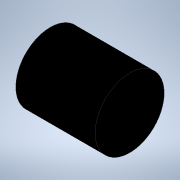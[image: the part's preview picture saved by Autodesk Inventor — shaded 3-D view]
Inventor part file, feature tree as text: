
AUTODESK INVENTOR PART (.ipt)
format: ipt  version: 2020 (Build 240168000, 168)  size: 92,160 bytes
history: native  units: mm
features: extrude x1, sketch x1
ambient origin geometry x8: Origin, YZ Plane, XZ Plane, XY Plane, X Axis, Y Axis, Z Axis, Center Point
bodies: Solid1 (feature_tree)
feature tree (2):
  extrude  "Extrusion1"  Depth=37.5mm TaperAngle=0.0deg
  sketch  "Sketch1"  dims[d0=32.6mm d1=37.5mm d2=0.0mm]
